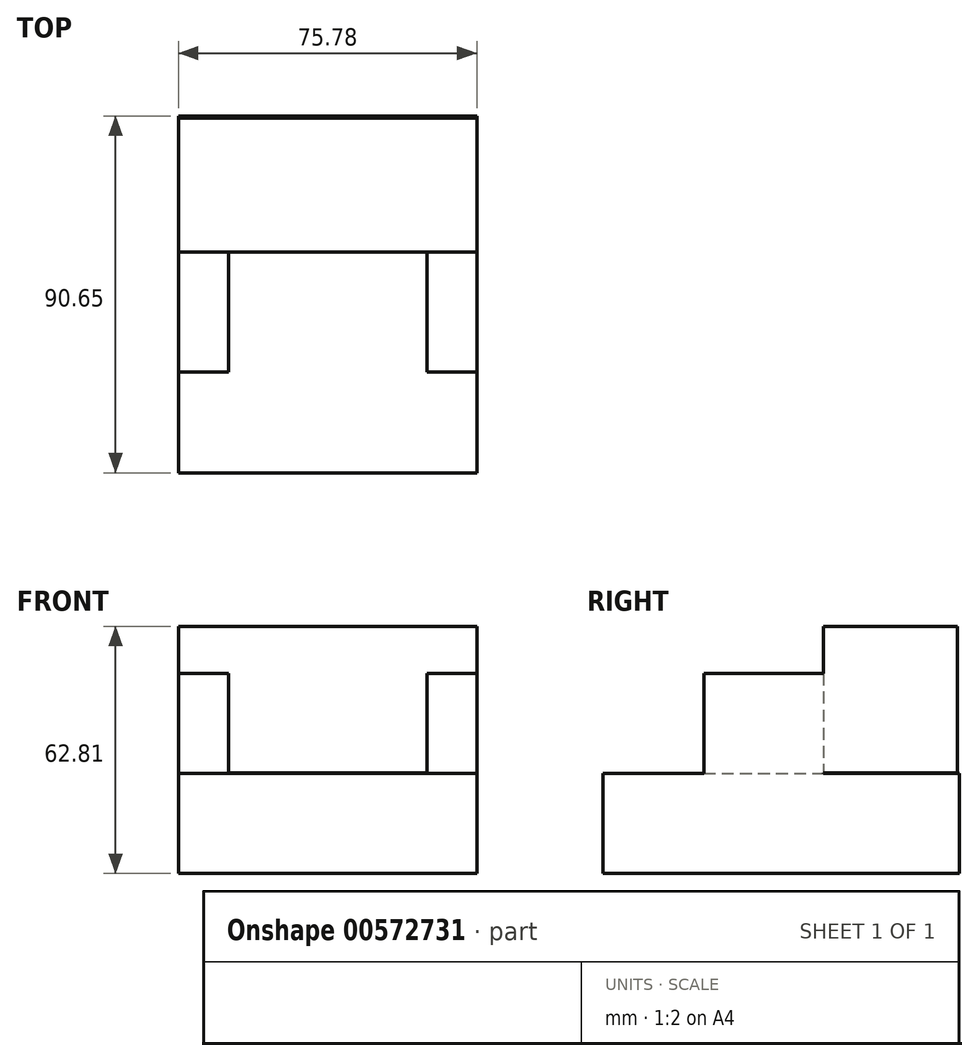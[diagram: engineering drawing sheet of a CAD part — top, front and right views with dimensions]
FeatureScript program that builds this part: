
annotation { "Feature Type Name" : "Feature", "Feature Type Description" : "" }
export const myFeature = defineFeature(function(context is Context, id is Id, definition is map)
    precondition{}
    {
        {
            var Q0;
            Q0=qCreatedBy(makeId("Top.planeOp"),FACE);
            var sketch = newSketch(context, id + "F0", { "sketchPlane" : qUnion([Q0])});
            skLineSegment(sketch, "E0.bottom", {"start": v(-36.43, 34.54) * mm, "end": v(39.35, 34.54) * mm});
            skLineSegment(sketch, "E0.top", {"start": v(-36.43, -56.1) * mm, "end": v(39.35, -56.1) * mm});
            skLineSegment(sketch, "E0.left", {"start": v(-36.43, 34.54) * mm, "end": v(-36.43, -56.1) * mm});
            skLineSegment(sketch, "E0.right", {"start": v(39.35, 34.54) * mm, "end": v(39.35, -56.1) * mm});
            skSolve(sketch);
        }
        {
            var Q0;
            Q0=makeQuery(id+"F0.imprint","IMPRINT",FACE,{"disambiguationData":[TD([[makeQuery(id+"F0.imprint","IMPRINT",EDGE,{"derivedFrom":sQuery(id+"F0.wireOp",EDGE,"E0.bottom")}),-1.0]])]});
            extrude(context, id + "F1", {"entities" : qUnion([Q0]), "depth" : 25.4 * mm, "offsetDistance" : 25.4 * mm});
        }
        {
            var Q0;
            Q0=qCreatedBy(makeId("Top.planeOp"),FACE);
            var sketch = newSketch(context, id + "F2", { "sketchPlane" : qUnion([Q0])});
            skLineSegment(sketch, "E1.bottom", {"start": v(-36.43, 0) * mm, "end": v(-23.73, 0) * mm});
            skLineSegment(sketch, "E1.top", {"start": v(-36.43, -30.48) * mm, "end": v(-23.73, -30.48) * mm});
            skLineSegment(sketch, "E1.left", {"start": v(-36.43, 0) * mm, "end": v(-36.43, -30.48) * mm});
            skLineSegment(sketch, "E1.right", {"start": v(-23.73, 0) * mm, "end": v(-23.73, -30.48) * mm});
            skLineSegment(sketch, "E2.bottom", {"start": v(39.35, 0) * mm, "end": v(26.65, 0) * mm});
            skLineSegment(sketch, "E2.top", {"start": v(39.35, -30.48) * mm, "end": v(26.65, -30.48) * mm});
            skLineSegment(sketch, "E2.left", {"start": v(39.35, 0) * mm, "end": v(39.35, -30.48) * mm});
            skLineSegment(sketch, "E2.right", {"start": v(26.65, 0) * mm, "end": v(26.65, -30.48) * mm});
            skSolve(sketch);
        }
        {
            var Q0;
            Q0 = qSketchRegion(id + "F2", true);
            extrude(context, id + "F3", {"entities" : qUnion([Q0]), "operationType" : NewBodyOperationType.ADD, "depth" : 50.8 * mm, "offsetDistance" : 25.4 * mm});
        }
        {
            var Q0;
            Q0=qCreatedBy(makeId("Front.planeOp"),FACE);
            var sketch = newSketch(context, id + "F4", { "sketchPlane" : qUnion([Q0])});
            skLineSegment(sketch, "E3.bottom", {"start": v(-36.43, 25.5) * mm, "end": v(39.35, 25.5) * mm});
            skLineSegment(sketch, "E3.top", {"start": v(-36.43, 62.81) * mm, "end": v(39.35, 62.81) * mm});
            skLineSegment(sketch, "E3.left", {"start": v(-36.43, 25.5) * mm, "end": v(-36.43, 62.81) * mm});
            skLineSegment(sketch, "E3.right", {"start": v(39.35, 25.5) * mm, "end": v(39.35, 62.81) * mm});
            skSolve(sketch);
        }
        {
            var Q0;
            Q0 = qSketchRegion(id + "F4", true);
            extrude(context, id + "F5", {"entities" : qUnion([Q0]), "operationType" : NewBodyOperationType.ADD, "oppositeDirection" : true, "depth" : 34.04 * mm, "offsetDistance" : 25.4 * mm});
        }
    });
